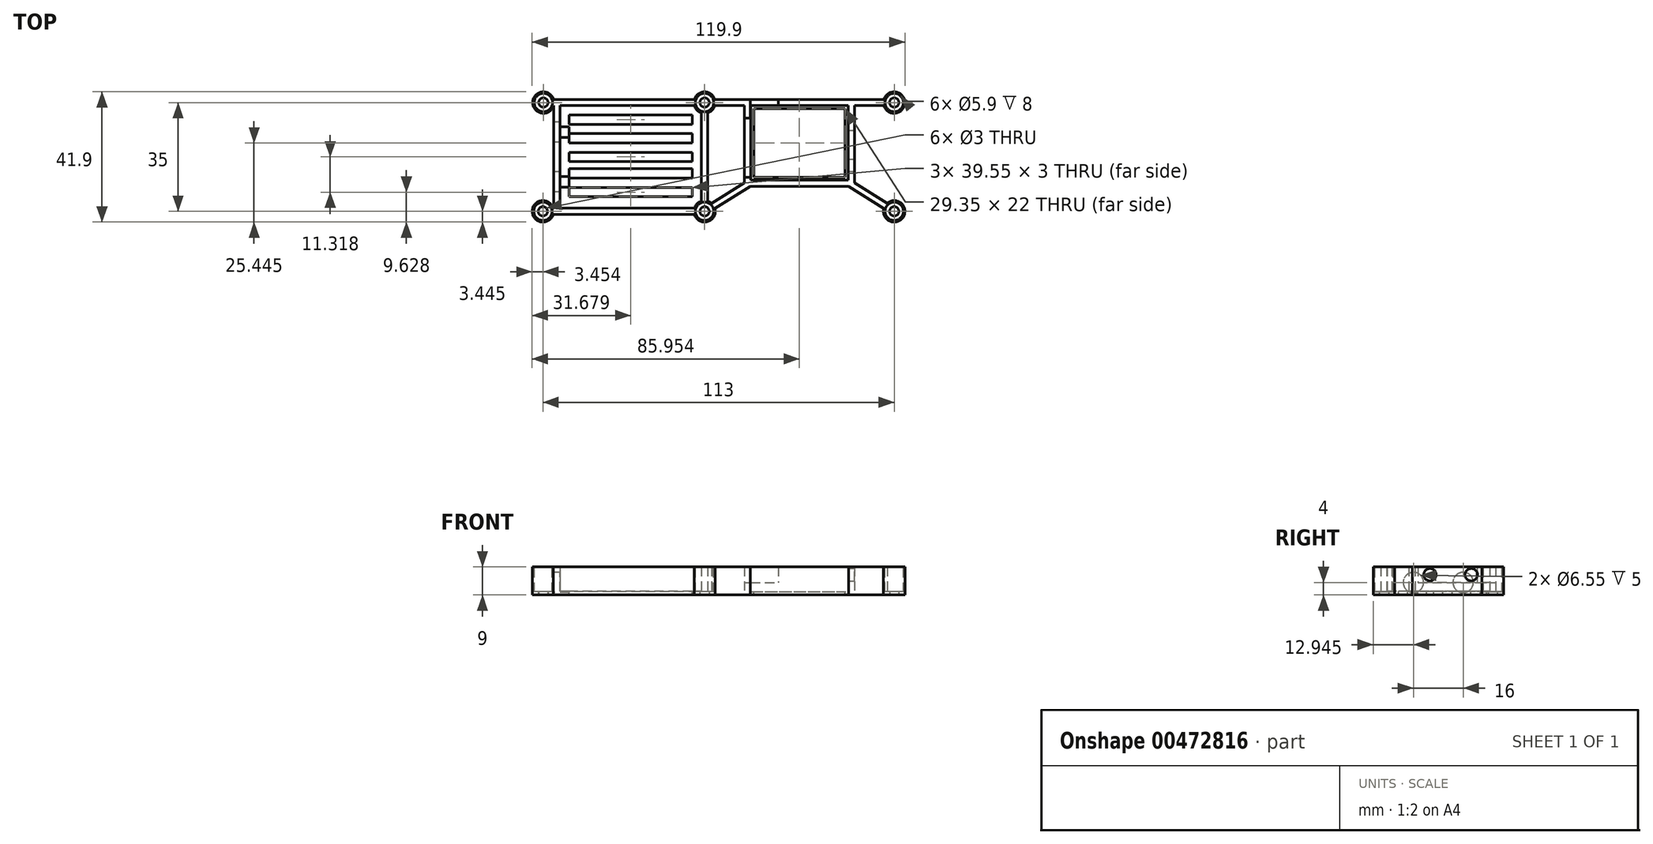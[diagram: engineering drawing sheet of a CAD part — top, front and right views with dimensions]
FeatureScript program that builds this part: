
annotation { "Feature Type Name" : "Feature", "Feature Type Description" : "" }
export const myFeature = defineFeature(function(context is Context, id is Id, definition is map)
    precondition{}
    {
        {
            var Q0;
            Q0=qCreatedBy(makeId("Top.planeOp"),FACE);
            var sketch = newSketch(context, id + "F0", { "sketchPlane" : qUnion([Q0])});
            skLineSegment(sketch, "E0.bottom", {"start": v(59.75, 20.2) * mm, "end": v(-53.1, 20.2) * mm, "construction": true});
            skLineSegment(sketch, "E0.top", {"start": v(59.75, -14.8) * mm, "end": v(-53.25, -14.8) * mm, "construction": true});
            skLineSegment(sketch, "E0.left", {"start": v(59.75, 20.2) * mm, "end": v(59.75, -14.8) * mm, "construction": true});
            skCircle(sketch, "E1", {"center": v(59.75, 20.2) * mm, "radius": 1.5 * mm});
            skCircle(sketch, "E2", {"center": v(59.75, -14.8) * mm, "radius": 1.5 * mm});
            skLineSegment(sketch, "E3.bottom", {"start": v(59.75, 20.2) * mm, "end": v(-1.25, 20.2) * mm, "construction": true});
            skLineSegment(sketch, "E3.top", {"start": v(59.75, -14.8) * mm, "end": v(-1.25, -14.8) * mm, "construction": true});
            skLineSegment(sketch, "E3.right", {"start": v(-1.25, 20.2) * mm, "end": v(-1.25, -14.8) * mm, "construction": true});
            skCircle(sketch, "E4", {"center": v(-1.25, 20.2) * mm, "radius": 1.5 * mm});
            skCircle(sketch, "E5", {"center": v(-1.25, -14.8) * mm, "radius": 1.5 * mm});
            skCircle(sketch, "E6", {"center": v(-53.1, 20.2) * mm, "radius": 1.5 * mm});
            skCircle(sketch, "E7", {"center": v(-53.25, -14.8) * mm, "radius": 1.5 * mm});
            skCircle(sketch, "E8", {"center": v(-1.25, 20.2) * mm, "radius": 3.45 * mm});
            skCircle(sketch, "E9", {"center": v(-1.25, -14.8) * mm, "radius": 3.45 * mm});
            skCircle(sketch, "E10", {"center": v(59.75, -14.8) * mm, "radius": 3.45 * mm});
            skCircle(sketch, "E11", {"center": v(-53.25, -14.8) * mm, "radius": 3.45 * mm});
            skCircle(sketch, "E12", {"center": v(-53.1, 20.2) * mm, "radius": 3.45 * mm});
            skCircle(sketch, "E13", {"center": v(59.75, 20.2) * mm, "radius": 3.45 * mm});
            skLineSegment(sketch, "E14.bottom", {"start": v(13.58, 19.2) * mm, "end": v(44.93, 19.2) * mm});
            skLineSegment(sketch, "E14.top", {"start": v(13.58, -4.8) * mm, "end": v(44.93, -4.8) * mm});
            skLineSegment(sketch, "E14.left", {"start": v(13.58, 19.2) * mm, "end": v(13.58, -4.8) * mm});
            skLineSegment(sketch, "E14.right", {"start": v(44.93, 19.2) * mm, "end": v(44.93, -4.8) * mm});
            skLineSegment(sketch, "E15", {"start": v(29.25, 20.2) * mm, "end": v(29.25, -14.8) * mm, "construction": true});
            skLineSegment(sketch, "E16.bottom", {"start": v(11.58, 21.2) * mm, "end": v(46.93, 21.2) * mm});
            skLineSegment(sketch, "E16.top", {"start": v(11.58, -6.8) * mm, "end": v(46.93, -6.8) * mm});
            skLineSegment(sketch, "E16.left", {"start": v(11.58, 21.2) * mm, "end": v(11.58, -6.8) * mm});
            skLineSegment(sketch, "E16.right", {"start": v(46.93, 21.2) * mm, "end": v(46.93, -6.8) * mm});
            skLineSegment(sketch, "E17", {"start": v(11.58, 21.2) * mm, "end": v(2.06, 21.2) * mm});
            skLineSegment(sketch, "E18", {"start": v(11.58, 19.2) * mm, "end": v(2.06, 19.2) * mm});
            skLineSegment(sketch, "E19", {"start": v(11.58, -5.63) * mm, "end": v(1.03, -12.2) * mm});
            skLineSegment(sketch, "E20", {"start": v(13.47, -6.8) * mm, "end": v(2.08, -13.9) * mm});
            skLineSegment(sketch, "E21", {"start": v(11.58, -6.8) * mm, "end": v(-1.25, -14.8) * mm, "construction": true});
            skLineSegment(sketch, "E22", {"start": v(59.75, -14.8) * mm, "end": v(46.93, -6.8) * mm, "construction": true});
            skLineSegment(sketch, "E23", {"start": v(46.93, -5.63) * mm, "end": v(57.48, -12.2) * mm});
            skLineSegment(sketch, "E24", {"start": v(45.04, -6.8) * mm, "end": v(56.42, -13.9) * mm});
            skLineSegment(sketch, "E25", {"start": v(46.93, 21.2) * mm, "end": v(56.45, 21.2) * mm});
            skLineSegment(sketch, "E26", {"start": v(44.93, 19.2) * mm, "end": v(56.45, 19.2) * mm});
            skLineSegment(sketch, "E27.bottom", {"start": v(-52.25, 19.2) * mm, "end": v(-2.25, 19.2) * mm});
            skLineSegment(sketch, "E27.top", {"start": v(-52.25, -13.8) * mm, "end": v(-2.36, -13.8) * mm});
            skLineSegment(sketch, "E27.right", {"start": v(-2.25, 19.2) * mm, "end": v(-2.25, -13.69) * mm});
            skLineSegment(sketch, "E28.bottom", {"start": v(-54.25, 21.2) * mm, "end": v(-0.25, 21.2) * mm});
            skLineSegment(sketch, "E28.top", {"start": v(-54.25, -15.8) * mm, "end": v(-0.25, -15.8) * mm});
            skLineSegment(sketch, "E28.right", {"start": v(-0.25, 21.2) * mm, "end": v(-0.25, -15.8) * mm});
            skLineSegment(sketch, "E29", {"start": v(-49.8, 19.2) * mm, "end": v(-49.8, -13.8) * mm});
            skLineSegment(sketch, "E30", {"start": v(-47.8, 19.2) * mm, "end": v(-47.8, -13.8) * mm});
            skCircle(sketch, "E31", {"center": v(-53.1, 20.2) * mm, "radius": 2.95 * mm});
            skCircle(sketch, "E32", {"center": v(-1.25, 20.2) * mm, "radius": 2.95 * mm});
            skCircle(sketch, "E33", {"center": v(59.75, 20.2) * mm, "radius": 2.95 * mm});
            skCircle(sketch, "E34", {"center": v(59.75, -14.8) * mm, "radius": 2.95 * mm});
            skCircle(sketch, "E35", {"center": v(-1.25, -14.8) * mm, "radius": 2.95 * mm});
            skCircle(sketch, "E36", {"center": v(-53.25, -14.8) * mm, "radius": 2.95 * mm});
            skSolve(sketch);
        }
        {
            var Q0;
            {var subQ1=sQuery(id+"F0.wireOp",EDGE,"E12");var subQ3=sQuery(id+"F0.wireOp",EDGE,"E28.bottom");var subQ4=makeQuery(id+"F0.imprint","INTERSECT",VERTEX,{"derivedFrom":[subQ1,subQ3]});Q0=makeQuery(id+"F0.imprint","IMPRINT",FACE,{"disambiguationData":[TD([[makeQuery(id+"F0.imprint","IMPRINT",EDGE,{"disambiguationData":[TD([[subQ4,1.0]])],"derivedFrom":subQ3}),1.0]])]});}
            var Q1;
            {var subQ1=sQuery(id+"F0.wireOp",EDGE,"E6");var subQ5=sQuery(id+"F0.wireOp",EDGE,"E28.bottom");var subQ7=makeQuery(id+"F0.imprint","INTERSECT",VERTEX,{"disambiguationData":[OD(0.0)],"derivedFrom":[subQ1,subQ5]});Q1=makeQuery(id+"F0.imprint","IMPRINT",FACE,{"disambiguationData":[TD([[makeQuery(id+"F0.imprint","IMPRINT",EDGE,{"disambiguationData":[TD([[subQ7,1.0]])],"derivedFrom":subQ1}),-1.0]])]});}
            var Q2;
            {var subQ0=sQuery(id+"F0.wireOp",EDGE,"E27.bottom");var subQ1=sQuery(id+"F0.wireOp",EDGE,"E6");var subQ2=makeQuery(id+"F0.imprint","INTERSECT",VERTEX,{"derivedFrom":[subQ1,subQ0]});Q2=makeQuery(id+"F0.imprint","IMPRINT",FACE,{"disambiguationData":[TD([[makeQuery(id+"F0.imprint","IMPRINT",EDGE,{"disambiguationData":[TD([[subQ2,-1.0]])],"derivedFrom":subQ1}),-1.0]])]});}
            var Q3;
            {var subQ1=sQuery(id+"F0.wireOp",EDGE,"E12");var subQ3=sQuery(id+"F0.wireOp",EDGE,"E28.bottom");var subQ4=makeQuery(id+"F0.imprint","INTERSECT",VERTEX,{"derivedFrom":[subQ1,subQ3]});Q3=makeQuery(id+"F0.imprint","IMPRINT",FACE,{"disambiguationData":[TD([[makeQuery(id+"F0.imprint","IMPRINT",EDGE,{"disambiguationData":[TD([[subQ4,1.0]])],"derivedFrom":subQ3}),-1.0]])]});}
            var Q4;
            {var subQ0=sQuery(id+"F0.wireOp",EDGE,"E29");Q4=makeQuery(id+"F0.imprint","IMPRINT",FACE,{"disambiguationData":[TD([[makeQuery(id+"F0.imprint","IMPRINT",EDGE,{"derivedFrom":subQ0}),1.0]])]});}
            var Q5;
            {var subQ2=sQuery(id+"F0.wireOp",EDGE,"E8");var subQ4=sQuery(id+"F0.wireOp",EDGE,"E28.bottom");var subQ5=makeQuery(id+"F0.imprint","INTERSECT",VERTEX,{"derivedFrom":[subQ2,subQ4]});Q5=makeQuery(id+"F0.imprint","IMPRINT",FACE,{"disambiguationData":[TD([[makeQuery(id+"F0.imprint","IMPRINT",EDGE,{"disambiguationData":[TD([[subQ5,-1.0]])],"derivedFrom":subQ2}),-1.0]])]});}
            var Q6;
            {var subQ0=sQuery(id+"F0.wireOp",EDGE,"E27.top");var subQ1=sQuery(id+"F0.wireOp",EDGE,"E7");var subQ2=makeQuery(id+"F0.imprint","INTERSECT",VERTEX,{"derivedFrom":[subQ1,subQ0]});Q6=makeQuery(id+"F0.imprint","IMPRINT",FACE,{"disambiguationData":[TD([[makeQuery(id+"F0.imprint","IMPRINT",EDGE,{"disambiguationData":[TD([[subQ2,-1.0]])],"derivedFrom":subQ1}),-1.0]])]});}
            var Q7;
            {var subQ0=sQuery(id+"F0.wireOp",EDGE,"E27.top");var subQ1=sQuery(id+"F0.wireOp",EDGE,"E11");var subQ2=makeQuery(id+"F0.imprint","INTERSECT",VERTEX,{"derivedFrom":[subQ1,subQ0]});Q7=makeQuery(id+"F0.imprint","IMPRINT",FACE,{"disambiguationData":[TD([[makeQuery(id+"F0.imprint","IMPRINT",EDGE,{"disambiguationData":[TD([[subQ2,-1.0]])],"derivedFrom":subQ1}),1.0]])]});}
            var Q8;
            {var subQ0=sQuery(id+"F0.wireOp",EDGE,"E27.top");var subQ1=sQuery(id+"F0.wireOp",EDGE,"E7");var subQ2=makeQuery(id+"F0.imprint","INTERSECT",VERTEX,{"derivedFrom":[subQ1,subQ0]});Q8=makeQuery(id+"F0.imprint","IMPRINT",FACE,{"disambiguationData":[TD([[makeQuery(id+"F0.imprint","IMPRINT",EDGE,{"disambiguationData":[TD([[subQ2,1.0]])],"derivedFrom":subQ1}),-1.0]])]});}
            var Q9;
            {var subQ5=sQuery(id+"F0.wireOp",EDGE,"E28.top");var subQ6=sQuery(id+"F0.wireOp",EDGE,"E9");var subQ7=makeQuery(id+"F0.imprint","INTERSECT",VERTEX,{"derivedFrom":[subQ6,subQ5]});Q9=makeQuery(id+"F0.imprint","IMPRINT",FACE,{"disambiguationData":[TD([[makeQuery(id+"F0.imprint","IMPRINT",EDGE,{"disambiguationData":[TD([[subQ7,1.0]])],"derivedFrom":subQ6}),-1.0]])]});}
            var Q10;
            {var subQ0=sQuery(id+"F0.wireOp",EDGE,"E27.top");var subQ1=sQuery(id+"F0.wireOp",EDGE,"E11");var subQ2=makeQuery(id+"F0.imprint","INTERSECT",VERTEX,{"derivedFrom":[subQ1,subQ0]});Q10=makeQuery(id+"F0.imprint","IMPRINT",FACE,{"disambiguationData":[TD([[makeQuery(id+"F0.imprint","IMPRINT",EDGE,{"disambiguationData":[TD([[subQ2,1.0]])],"derivedFrom":subQ1}),1.0]])]});}
            var Q11;
            {var subQ0=sQuery(id+"F0.wireOp",EDGE,"E27.right");var subQ1=sQuery(id+"F0.wireOp",EDGE,"E8");var subQ2=makeQuery(id+"F0.imprint","INTERSECT",VERTEX,{"derivedFrom":[subQ1,subQ0]});Q11=makeQuery(id+"F0.imprint","IMPRINT",FACE,{"disambiguationData":[TD([[makeQuery(id+"F0.imprint","IMPRINT",EDGE,{"disambiguationData":[TD([[subQ2,-1.0]])],"derivedFrom":subQ1}),-1.0]])]});}
            var Q12;
            {var subQ0=sQuery(id+"F0.wireOp",EDGE,"E17");Q12=makeQuery(id+"F0.imprint","IMPRINT",FACE,{"disambiguationData":[TD([[makeQuery(id+"F0.imprint","IMPRINT",EDGE,{"derivedFrom":subQ0}),1.0]])]});}
            var Q13;
            Q13=makeQuery(id+"F0.imprint","IMPRINT",FACE,{"disambiguationData":[TD([[makeQuery(id+"F0.imprint","IMPRINT",EDGE,{"derivedFrom":sQuery(id+"F0.wireOp",EDGE,"E14.bottom")}),1.0]])]});
            var Q14;
            {var subQ3=sQuery(id+"F0.wireOp",EDGE,"E19");Q14=makeQuery(id+"F0.imprint","IMPRINT",FACE,{"disambiguationData":[TD([[makeQuery(id+"F0.imprint","IMPRINT",EDGE,{"derivedFrom":subQ3}),1.0]])]});}
            var Q15;
            {var subQ0=sQuery(id+"F0.wireOp",EDGE,"E28.right");var subQ1=sQuery(id+"F0.wireOp",EDGE,"E5");var subQ2=makeQuery(id+"F0.imprint","INTERSECT",VERTEX,{"derivedFrom":[subQ1,subQ0]});Q15=makeQuery(id+"F0.imprint","IMPRINT",FACE,{"disambiguationData":[TD([[makeQuery(id+"F0.imprint","IMPRINT",EDGE,{"disambiguationData":[TD([[subQ2,1.0]])],"derivedFrom":subQ1}),-1.0]])]});}
            var Q16;
            {var subQ1=sQuery(id+"F0.wireOp",EDGE,"E9");var subQ5=makeQuery(id+"F0.imprint","INTERSECT",VERTEX,{"derivedFrom":[subQ1,sQuery(id+"F0.wireOp",EDGE,"E19")]});Q16=makeQuery(id+"F0.imprint","IMPRINT",FACE,{"disambiguationData":[TD([[makeQuery(id+"F0.imprint","IMPRINT",EDGE,{"disambiguationData":[TD([[subQ5,1.0]])],"derivedFrom":subQ1}),1.0]])]});}
            var Q17;
            {var subQ0=sQuery(id+"F0.wireOp",EDGE,"E27.right");var subQ1=sQuery(id+"F0.wireOp",EDGE,"E5");var subQ2=makeQuery(id+"F0.imprint","INTERSECT",VERTEX,{"derivedFrom":[subQ1,subQ0]});Q17=makeQuery(id+"F0.imprint","IMPRINT",FACE,{"disambiguationData":[TD([[makeQuery(id+"F0.imprint","IMPRINT",EDGE,{"disambiguationData":[TD([[subQ2,1.0]])],"derivedFrom":subQ1}),-1.0]])]});}
            var Q18;
            {var subQ0=sQuery(id+"F0.wireOp",EDGE,"E27.right");var subQ1=sQuery(id+"F0.wireOp",EDGE,"E9");var subQ2=makeQuery(id+"F0.imprint","INTERSECT",VERTEX,{"derivedFrom":[subQ1,subQ0]});Q18=makeQuery(id+"F0.imprint","IMPRINT",FACE,{"disambiguationData":[TD([[makeQuery(id+"F0.imprint","IMPRINT",EDGE,{"disambiguationData":[TD([[subQ2,-1.0]])],"derivedFrom":subQ1}),1.0]])]});}
            var Q19;
            {var subQ0=sQuery(id+"F0.wireOp",EDGE,"E28.right");var subQ1=sQuery(id+"F0.wireOp",EDGE,"E9");var subQ2=makeQuery(id+"F0.imprint","INTERSECT",VERTEX,{"derivedFrom":[subQ1,subQ0]});Q19=makeQuery(id+"F0.imprint","IMPRINT",FACE,{"disambiguationData":[TD([[makeQuery(id+"F0.imprint","IMPRINT",EDGE,{"disambiguationData":[TD([[subQ2,-1.0]])],"derivedFrom":subQ1}),1.0]])]});}
            var Q20;
            {var subQ0=sQuery(id+"F0.wireOp",EDGE,"E27.right");var subQ1=sQuery(id+"F0.wireOp",EDGE,"E5");var subQ2=makeQuery(id+"F0.imprint","INTERSECT",VERTEX,{"derivedFrom":[subQ1,subQ0]});Q20=makeQuery(id+"F0.imprint","IMPRINT",FACE,{"disambiguationData":[TD([[makeQuery(id+"F0.imprint","IMPRINT",EDGE,{"disambiguationData":[TD([[subQ2,-1.0]])],"derivedFrom":subQ1}),-1.0]])]});}
            var Q21;
            {var subQ0=sQuery(id+"F0.wireOp",EDGE,"E27.top");var subQ1=sQuery(id+"F0.wireOp",EDGE,"E5");var subQ2=makeQuery(id+"F0.imprint","INTERSECT",VERTEX,{"derivedFrom":[subQ1,subQ0]});Q21=makeQuery(id+"F0.imprint","IMPRINT",FACE,{"disambiguationData":[TD([[makeQuery(id+"F0.imprint","IMPRINT",EDGE,{"disambiguationData":[TD([[subQ2,-1.0]])],"derivedFrom":subQ1}),-1.0]])]});}
            var Q22;
            {var subQ0=sQuery(id+"F0.wireOp",EDGE,"E28.top");var subQ1=sQuery(id+"F0.wireOp",EDGE,"E9");var subQ2=makeQuery(id+"F0.imprint","INTERSECT",VERTEX,{"derivedFrom":[subQ1,subQ0]});Q22=makeQuery(id+"F0.imprint","IMPRINT",FACE,{"disambiguationData":[TD([[makeQuery(id+"F0.imprint","IMPRINT",EDGE,{"disambiguationData":[TD([[subQ2,1.0]])],"derivedFrom":subQ1}),1.0]])]});}
            var Q23;
            {var subQ0=sQuery(id+"F0.wireOp",EDGE,"E28.bottom");var subQ1=sQuery(id+"F0.wireOp",EDGE,"E4");var subQ2=makeQuery(id+"F0.imprint","INTERSECT",VERTEX,{"derivedFrom":[subQ1,subQ0]});Q23=makeQuery(id+"F0.imprint","IMPRINT",FACE,{"disambiguationData":[TD([[makeQuery(id+"F0.imprint","IMPRINT",EDGE,{"disambiguationData":[TD([[subQ2,1.0]])],"derivedFrom":subQ1}),-1.0]])]});}
            var Q24;
            {var subQ1=sQuery(id+"F0.wireOp",EDGE,"E8");var subQ9=makeQuery(id+"F0.imprint","INTERSECT",VERTEX,{"derivedFrom":[subQ1,sQuery(id+"F0.wireOp",EDGE,"E17")]});Q24=makeQuery(id+"F0.imprint","IMPRINT",FACE,{"disambiguationData":[TD([[makeQuery(id+"F0.imprint","IMPRINT",EDGE,{"disambiguationData":[TD([[subQ9,-1.0]])],"derivedFrom":subQ1}),1.0]])]});}
            var Q25;
            {var subQ0=sQuery(id+"F0.wireOp",EDGE,"E27.bottom");var subQ1=sQuery(id+"F0.wireOp",EDGE,"E8");var subQ2=makeQuery(id+"F0.imprint","INTERSECT",VERTEX,{"derivedFrom":[subQ1,subQ0]});Q25=makeQuery(id+"F0.imprint","IMPRINT",FACE,{"disambiguationData":[TD([[makeQuery(id+"F0.imprint","IMPRINT",EDGE,{"disambiguationData":[TD([[subQ2,-1.0]])],"derivedFrom":subQ1}),1.0]])]});}
            var Q26;
            {var subQ0=sQuery(id+"F0.wireOp",EDGE,"E28.bottom");var subQ1=sQuery(id+"F0.wireOp",EDGE,"E8");var subQ2=makeQuery(id+"F0.imprint","INTERSECT",VERTEX,{"derivedFrom":[subQ1,subQ0]});Q26=makeQuery(id+"F0.imprint","IMPRINT",FACE,{"disambiguationData":[TD([[makeQuery(id+"F0.imprint","IMPRINT",EDGE,{"disambiguationData":[TD([[subQ2,-1.0]])],"derivedFrom":subQ1}),1.0]])]});}
            var Q27;
            {var subQ0=sQuery(id+"F0.wireOp",EDGE,"E27.bottom");var subQ1=sQuery(id+"F0.wireOp",EDGE,"E4");var subQ2=makeQuery(id+"F0.imprint","INTERSECT",VERTEX,{"derivedFrom":[subQ1,subQ0]});Q27=makeQuery(id+"F0.imprint","IMPRINT",FACE,{"disambiguationData":[TD([[makeQuery(id+"F0.imprint","IMPRINT",EDGE,{"disambiguationData":[TD([[subQ2,1.0]])],"derivedFrom":subQ1}),-1.0]])]});}
            var Q28;
            {var subQ0=sQuery(id+"F0.wireOp",EDGE,"E27.bottom");var subQ1=sQuery(id+"F0.wireOp",EDGE,"E4");var subQ2=makeQuery(id+"F0.imprint","INTERSECT",VERTEX,{"derivedFrom":[subQ1,subQ0]});Q28=makeQuery(id+"F0.imprint","IMPRINT",FACE,{"disambiguationData":[TD([[makeQuery(id+"F0.imprint","IMPRINT",EDGE,{"disambiguationData":[TD([[subQ2,-1.0]])],"derivedFrom":subQ1}),-1.0]])]});}
            var Q29;
            {var subQ0=sQuery(id+"F0.wireOp",EDGE,"E27.right");var subQ1=sQuery(id+"F0.wireOp",EDGE,"E4");var subQ2=makeQuery(id+"F0.imprint","INTERSECT",VERTEX,{"derivedFrom":[subQ1,subQ0]});Q29=makeQuery(id+"F0.imprint","IMPRINT",FACE,{"disambiguationData":[TD([[makeQuery(id+"F0.imprint","IMPRINT",EDGE,{"disambiguationData":[TD([[subQ2,-1.0]])],"derivedFrom":subQ1}),-1.0]])]});}
            var Q30;
            {var subQ0=sQuery(id+"F0.wireOp",EDGE,"E27.right");var subQ1=sQuery(id+"F0.wireOp",EDGE,"E8");var subQ2=makeQuery(id+"F0.imprint","INTERSECT",VERTEX,{"derivedFrom":[subQ1,subQ0]});Q30=makeQuery(id+"F0.imprint","IMPRINT",FACE,{"disambiguationData":[TD([[makeQuery(id+"F0.imprint","IMPRINT",EDGE,{"disambiguationData":[TD([[subQ2,-1.0]])],"derivedFrom":subQ1}),1.0]])]});}
            var Q31;
            {var subQ0=sQuery(id+"F0.wireOp",EDGE,"E25");Q31=makeQuery(id+"F0.imprint","IMPRINT",FACE,{"disambiguationData":[TD([[makeQuery(id+"F0.imprint","IMPRINT",EDGE,{"derivedFrom":subQ0}),-1.0]])]});}
            var Q32;
            Q32=makeQuery(id+"F0.imprint","IMPRINT",FACE,{"disambiguationData":[TD([[makeQuery(id+"F0.imprint","IMPRINT",EDGE,{"derivedFrom":sQuery(id+"F0.wireOp",EDGE,"E1")}),-1.0]])]});
            var Q33;
            Q33=makeQuery(id+"F0.imprint","IMPRINT",FACE,{"disambiguationData":[TD([[makeQuery(id+"F0.imprint","IMPRINT",EDGE,{"derivedFrom":sQuery(id+"F0.wireOp",EDGE,"E33")}),-1.0]])]});
            var Q34;
            {var subQ0=sQuery(id+"F0.wireOp",EDGE,"E23");Q34=makeQuery(id+"F0.imprint","IMPRINT",FACE,{"disambiguationData":[TD([[makeQuery(id+"F0.imprint","IMPRINT",EDGE,{"derivedFrom":subQ0}),-1.0]])]});}
            var Q35;
            Q35=makeQuery(id+"F0.imprint","IMPRINT",FACE,{"disambiguationData":[TD([[makeQuery(id+"F0.imprint","IMPRINT",EDGE,{"derivedFrom":sQuery(id+"F0.wireOp",EDGE,"E2")}),-1.0]])]});
            var Q36;
            Q36=makeQuery(id+"F0.imprint","IMPRINT",FACE,{"disambiguationData":[TD([[makeQuery(id+"F0.imprint","IMPRINT",EDGE,{"derivedFrom":sQuery(id+"F0.wireOp",EDGE,"E34")}),-1.0]])]});
            var Q37;
            Q37=makeQuery(id+"F0.imprint","IMPRINT",FACE,{"disambiguationData":[TD([[makeQuery(id+"F0.imprint","IMPRINT",EDGE,{"derivedFrom":sQuery(id+"F0.wireOp",EDGE,"E2")}),1.0]])]});
            var Q38;
            Q38=makeQuery(id+"F0.imprint","IMPRINT",FACE,{"disambiguationData":[TD([[makeQuery(id+"F0.imprint","IMPRINT",EDGE,{"derivedFrom":sQuery(id+"F0.wireOp",EDGE,"E1")}),1.0]])]});
            var Q39;
            {var subQ0=sQuery(id+"F0.wireOp",EDGE,"E27.right");var subQ3=sQuery(id+"F0.wireOp",EDGE,"E5");var subQ4=makeQuery(id+"F0.imprint","INTERSECT",VERTEX,{"derivedFrom":[subQ3,subQ0]});Q39=makeQuery(id+"F0.imprint","IMPRINT",FACE,{"disambiguationData":[TD([[makeQuery(id+"F0.imprint","IMPRINT",EDGE,{"disambiguationData":[TD([[subQ4,1.0]])],"derivedFrom":subQ3}),1.0]])]});}
            var Q40;
            {var subQ0=sQuery(id+"F0.wireOp",EDGE,"E28.right");var subQ1=sQuery(id+"F0.wireOp",EDGE,"E5");var subQ2=makeQuery(id+"F0.imprint","INTERSECT",VERTEX,{"derivedFrom":[subQ1,subQ0]});Q40=makeQuery(id+"F0.imprint","IMPRINT",FACE,{"disambiguationData":[TD([[makeQuery(id+"F0.imprint","IMPRINT",EDGE,{"disambiguationData":[TD([[subQ2,1.0]])],"derivedFrom":subQ1}),1.0]])]});}
            var Q41;
            {var subQ1=sQuery(id+"F0.wireOp",EDGE,"E27.bottom");var subQ3=sQuery(id+"F0.wireOp",EDGE,"E4");var subQ4=makeQuery(id+"F0.imprint","INTERSECT",VERTEX,{"derivedFrom":[subQ3,subQ1]});Q41=makeQuery(id+"F0.imprint","IMPRINT",FACE,{"disambiguationData":[TD([[makeQuery(id+"F0.imprint","IMPRINT",EDGE,{"disambiguationData":[TD([[subQ4,1.0]])],"derivedFrom":subQ3}),1.0]])]});}
            var Q42;
            {var subQ0=sQuery(id+"F0.wireOp",EDGE,"E28.bottom");var subQ1=sQuery(id+"F0.wireOp",EDGE,"E4");var subQ2=makeQuery(id+"F0.imprint","INTERSECT",VERTEX,{"derivedFrom":[subQ1,subQ0]});Q42=makeQuery(id+"F0.imprint","IMPRINT",FACE,{"disambiguationData":[TD([[makeQuery(id+"F0.imprint","IMPRINT",EDGE,{"disambiguationData":[TD([[subQ2,1.0]])],"derivedFrom":subQ1}),1.0]])]});}
            var Q43;
            {var subQ0=sQuery(id+"F0.wireOp",EDGE,"E27.bottom");var subQ1=sQuery(id+"F0.wireOp",EDGE,"E4");var subQ2=makeQuery(id+"F0.imprint","INTERSECT",VERTEX,{"derivedFrom":[subQ1,subQ0]});Q43=makeQuery(id+"F0.imprint","IMPRINT",FACE,{"disambiguationData":[TD([[makeQuery(id+"F0.imprint","IMPRINT",EDGE,{"disambiguationData":[TD([[subQ2,-1.0]])],"derivedFrom":subQ1}),1.0]])]});}
            var Q44;
            {var subQ0=sQuery(id+"F0.wireOp",EDGE,"E28.bottom");var subQ1=sQuery(id+"F0.wireOp",EDGE,"E6");var subQ2=makeQuery(id+"F0.imprint","INTERSECT",VERTEX,{"disambiguationData":[OD(0.0)],"derivedFrom":[subQ1,subQ0]});Q44=makeQuery(id+"F0.imprint","IMPRINT",FACE,{"disambiguationData":[TD([[makeQuery(id+"F0.imprint","IMPRINT",EDGE,{"disambiguationData":[TD([[subQ2,-1.0]])],"derivedFrom":subQ1}),1.0]])]});}
            var Q45;
            {var subQ0=sQuery(id+"F0.wireOp",EDGE,"E28.bottom");var subQ1=sQuery(id+"F0.wireOp",EDGE,"E6");var subQ2=makeQuery(id+"F0.imprint","INTERSECT",VERTEX,{"disambiguationData":[OD(0.0)],"derivedFrom":[subQ1,subQ0]});Q45=makeQuery(id+"F0.imprint","IMPRINT",FACE,{"disambiguationData":[TD([[makeQuery(id+"F0.imprint","IMPRINT",EDGE,{"disambiguationData":[TD([[subQ2,1.0]])],"derivedFrom":subQ1}),1.0]])]});}
            var Q46;
            {var subQ0=sQuery(id+"F0.wireOp",EDGE,"E7");var subQ1=makeQuery(id+"F0.imprint","INTERSECT",VERTEX,{"derivedFrom":[subQ0,sQuery(id+"F0.wireOp",EDGE,"E27.top")]});Q46=makeQuery(id+"F0.imprint","IMPRINT",FACE,{"disambiguationData":[TD([[makeQuery(id+"F0.imprint","IMPRINT",EDGE,{"disambiguationData":[TD([[subQ1,-1.0]])],"derivedFrom":subQ0}),1.0]])]});}
            extrude(context, id + "F1", {"entities" : qUnion([Q0, Q1, Q2, Q3, Q4, Q5, Q6, Q7, Q8, Q9, Q10, Q11, Q12, Q13, Q14, Q15, Q16, Q17, Q18, Q19, Q20, Q21, Q22, Q23, Q24, Q25, Q26, Q27, Q28, Q29, Q30, Q31, Q32, Q33, Q34, Q35, Q36, Q37, Q38, Q39, Q40, Q41, Q42, Q43, Q44, Q45, Q46]), "depth" : 9 * mm});
        }
        {
            var Q0;
            Q0=makeQuery(id+"F0.imprint","IMPRINT",FACE,{"disambiguationData":[TD([[makeQuery(id+"F0.imprint","IMPRINT",EDGE,{"derivedFrom":sQuery(id+"F0.wireOp",EDGE,"E14.bottom")}),-1.0]])]});
            extrude(context, id + "F2", {"entities" : qUnion([Q0]), "operationType" : NewBodyOperationType.ADD, "depth" : 1 * mm});
        }
        {
            var Q0;
            Q0=makeQuery(id+"F2.opExtrude","CAP_FACE",FACE,{"disambiguationData":[OSD([sQuery(id+"F0.wireOp",EDGE,"E14.bottom"),sQuery(id+"F0.wireOp",EDGE,"E14.top"),sQuery(id+"F0.wireOp",EDGE,"E14.left"),sQuery(id+"F0.wireOp",EDGE,"E14.right")])],"isStart":false});
            var sketch = newSketch(context, id + "F3", { "sketchPlane" : qUnion([Q0])});
            skLineSegment(sketch, "E37.bottom", {"start": v(14.58, 18.2) * mm, "end": v(43.93, 18.2) * mm});
            skLineSegment(sketch, "E37.top", {"start": v(14.58, -3.8) * mm, "end": v(43.93, -3.8) * mm});
            skLineSegment(sketch, "E37.left", {"start": v(14.58, 18.2) * mm, "end": v(14.58, -3.8) * mm});
            skLineSegment(sketch, "E37.right", {"start": v(43.93, 18.2) * mm, "end": v(43.93, -3.8) * mm});
            skSolve(sketch);
        }
        {
            var Q0;
            Q0=makeQuery(id+"F3.imprint","IMPRINT",FACE,{"disambiguationData":[TD([[makeQuery(id+"F3.imprint","IMPRINT",EDGE,{"derivedFrom":sQuery(id+"F3.wireOp",EDGE,"E37.bottom")}),-1.0]])]});
            extrude(context, id + "F4", {"entities" : qUnion([Q0]), "operationType" : NewBodyOperationType.REMOVE, "oppositeDirection" : true, "depth" : 25 * mm});
        }
        {
            var Q0;
            {var subQ0=sQuery(id+"F0.wireOp",EDGE,"E30");Q0=makeQuery(id+"F0.imprint","IMPRINT",FACE,{"disambiguationData":[TD([[makeQuery(id+"F0.imprint","IMPRINT",EDGE,{"derivedFrom":subQ0}),1.0]])]});}
            extrude(context, id + "F5", {"entities" : qUnion([Q0]), "operationType" : NewBodyOperationType.ADD, "depth" : 1.2 * mm});
        }
        {
            var Q0;
            Q0=makeQuery(id+"F5.opExtrude","CAP_FACE",FACE,{"disambiguationData":[OSD([sQuery(id+"F0.wireOp",EDGE,"E8"),sQuery(id+"F0.wireOp",EDGE,"E9"),sQuery(id+"F0.wireOp",EDGE,"E27.bottom"),sQuery(id+"F0.wireOp",EDGE,"E27.top"),sQuery(id+"F0.wireOp",EDGE,"E27.right"),sQuery(id+"F0.wireOp",EDGE,"E30")])],"isStart":false});
            var sketch = newSketch(context, id + "F6", { "sketchPlane" : qUnion([Q0])});
            skLineSegment(sketch, "E38.bottom", {"start": v(-44.8, 16.2) * mm, "end": v(-5.25, 16.2) * mm});
            skLineSegment(sketch, "E38.top", {"start": v(-44.8, 13.2) * mm, "end": v(-5.25, 13.2) * mm});
            skLineSegment(sketch, "E38.left", {"start": v(-44.8, 16.2) * mm, "end": v(-44.8, 13.2) * mm});
            skLineSegment(sketch, "E38.right", {"start": v(-5.25, 16.2) * mm, "end": v(-5.25, 13.2) * mm});
            skLineSegment(sketch, "E39.bottom", {"start": v(-5.25, 10.2) * mm, "end": v(-44.8, 10.2) * mm});
            skLineSegment(sketch, "E39.top", {"start": v(-5.25, 7.2) * mm, "end": v(-44.8, 7.2) * mm});
            skLineSegment(sketch, "E39.left", {"start": v(-5.25, 10.2) * mm, "end": v(-5.25, 7.2) * mm});
            skLineSegment(sketch, "E39.right", {"start": v(-44.8, 10.2) * mm, "end": v(-44.8, 7.2) * mm});
            skLineSegment(sketch, "E40.bottom", {"start": v(-5.25, 4.2) * mm, "end": v(-44.8, 4.2) * mm});
            skLineSegment(sketch, "E40.top", {"start": v(-5.25, 1.2) * mm, "end": v(-44.8, 1.2) * mm});
            skLineSegment(sketch, "E40.left", {"start": v(-5.25, 4.2) * mm, "end": v(-5.25, 1.2) * mm});
            skLineSegment(sketch, "E40.right", {"start": v(-44.8, 4.2) * mm, "end": v(-44.8, 1.2) * mm});
            skLineSegment(sketch, "E41.bottom", {"start": v(-5.25, -1.12) * mm, "end": v(-44.8, -1.12) * mm});
            skLineSegment(sketch, "E41.top", {"start": v(-5.25, -4.12) * mm, "end": v(-44.8, -4.12) * mm});
            skLineSegment(sketch, "E41.left", {"start": v(-5.25, -1.12) * mm, "end": v(-5.25, -4.12) * mm});
            skLineSegment(sketch, "E41.right", {"start": v(-44.8, -1.12) * mm, "end": v(-44.8, -4.12) * mm});
            skLineSegment(sketch, "E42.bottom", {"start": v(-5.25, -7.12) * mm, "end": v(-44.8, -7.12) * mm});
            skLineSegment(sketch, "E42.top", {"start": v(-5.25, -10.12) * mm, "end": v(-44.8, -10.12) * mm});
            skLineSegment(sketch, "E42.left", {"start": v(-5.25, -7.12) * mm, "end": v(-5.25, -10.12) * mm});
            skLineSegment(sketch, "E42.right", {"start": v(-44.8, -7.12) * mm, "end": v(-44.8, -10.12) * mm});
            skSolve(sketch);
        }
        {
            var Q0;
            Q0=makeQuery(id+"F6.imprint","IMPRINT",FACE,{"disambiguationData":[TD([[makeQuery(id+"F6.imprint","IMPRINT",EDGE,{"derivedFrom":sQuery(id+"F6.wireOp",EDGE,"E38.bottom")}),-1.0]])]});
            var Q1;
            Q1=makeQuery(id+"F6.imprint","IMPRINT",FACE,{"disambiguationData":[TD([[makeQuery(id+"F6.imprint","IMPRINT",EDGE,{"derivedFrom":sQuery(id+"F6.wireOp",EDGE,"E39.bottom")}),1.0]])]});
            var Q2;
            Q2=makeQuery(id+"F6.imprint","IMPRINT",FACE,{"disambiguationData":[TD([[makeQuery(id+"F6.imprint","IMPRINT",EDGE,{"derivedFrom":sQuery(id+"F6.wireOp",EDGE,"E40.bottom")}),1.0]])]});
            var Q3;
            Q3=makeQuery(id+"F6.imprint","IMPRINT",FACE,{"disambiguationData":[TD([[makeQuery(id+"F6.imprint","IMPRINT",EDGE,{"derivedFrom":sQuery(id+"F6.wireOp",EDGE,"E41.bottom")}),1.0]])]});
            var Q4;
            Q4=makeQuery(id+"F6.imprint","IMPRINT",FACE,{"disambiguationData":[TD([[makeQuery(id+"F6.imprint","IMPRINT",EDGE,{"derivedFrom":sQuery(id+"F6.wireOp",EDGE,"E42.bottom")}),1.0]])]});
            extrude(context, id + "F7", {"entities" : qUnion([Q0, Q1, Q2, Q3, Q4]), "operationType" : NewBodyOperationType.REMOVE, "oppositeDirection" : true, "depth" : 25 * mm});
        }
        {
            var Q0;
            Q0=makeQuery(id+"F1.opExtrude","SWEPT_FACE",FACE,{"disambiguationData":[OSD([sQuery(id+"F0.wireOp",EDGE,"E16.right")])]});
            var sketch = newSketch(context, id + "F8", { "sketchPlane" : qUnion([Q0])});
            skLineSegment(sketch, "E43", {"start": v(-5.63, 6.5) * mm, "end": v(19.2, 6.5) * mm, "construction": true});
            skLineSegment(sketch, "E44", {"start": v(-5.63, 6.5) * mm, "end": v(0, 6.5) * mm, "construction": true});
            skLineSegment(sketch, "E45", {"start": v(19.2, 6.5) * mm, "end": v(13.3, 6.5) * mm, "construction": true});
            skCircle(sketch, "E46", {"center": v(0, 6.5) * mm, "radius": 2 * mm});
            skCircle(sketch, "E47", {"center": v(13.3, 6.5) * mm, "radius": 2 * mm});
            skSolve(sketch);
        }
        {
            var Q0;
            Q0=makeQuery(id+"F8.imprint","IMPRINT",FACE,{"disambiguationData":[TD([[makeQuery(id+"F8.imprint","IMPRINT",EDGE,{"derivedFrom":sQuery(id+"F8.wireOp",EDGE,"E47")}),1.0]])]});
            var Q1;
            Q1=makeQuery(id+"F8.imprint","IMPRINT",FACE,{"disambiguationData":[TD([[makeQuery(id+"F8.imprint","IMPRINT",EDGE,{"derivedFrom":sQuery(id+"F8.wireOp",EDGE,"E46")}),1.0]])]});
            extrude(context, id + "F9", {"entities" : qUnion([Q0, Q1]), "operationType" : NewBodyOperationType.REMOVE, "oppositeDirection" : true, "depth" : 4 * mm});
        }
        {
            var Q0;
            Q0=makeQuery(id+"F1.opExtrude","SWEPT_FACE",FACE,{"disambiguationData":[OSD([sQuery(id+"F0.wireOp",EDGE,"E29")])]});
            var sketch = newSketch(context, id + "F10", { "sketchPlane" : qUnion([Q0])});
            skLineSegment(sketch, "E48", {"start": v(-2.7, 9) * mm, "end": v(-2.7, 0) * mm, "construction": true});
            skLineSegment(sketch, "E49", {"start": v(-10.7, 4) * mm, "end": v(5.3, 4) * mm, "construction": true});
            skCircle(sketch, "E50", {"center": v(-10.7, 4) * mm, "radius": 3.28 * mm});
            skCircle(sketch, "E51", {"center": v(5.3, 4) * mm, "radius": 3.28 * mm});
            skSolve(sketch);
        }
        {
            var Q0;
            Q0 = qSketchRegion(id + "F10", true);
            extrude(context, id + "F11", {"entities" : qUnion([Q0]), "operationType" : NewBodyOperationType.REMOVE, "oppositeDirection" : true, "depth" : 5 * mm});
        }
        {
            var Q0;
            Q0=makeQuery(id+"F10.imprint","IMPRINT",FACE,{"disambiguationData":[TD([[makeQuery(id+"F10.imprint","IMPRINT",EDGE,{"derivedFrom":sQuery(id+"F10.wireOp",EDGE,"E50")}),1.0]])]});
            var Q1;
            Q1=makeQuery(id+"F10.imprint","IMPRINT",FACE,{"disambiguationData":[TD([[makeQuery(id+"F10.imprint","IMPRINT",EDGE,{"derivedFrom":sQuery(id+"F10.wireOp",EDGE,"E51")}),1.0]])]});
            extrude(context, id + "F12", {"entities" : qUnion([Q0, Q1]), "operationType" : NewBodyOperationType.REMOVE, "oppositeDirection" : true, "depth" : 4 * mm});
        }
        {
            var Q0;
            {var subQ1=sQuery(id+"F0.wireOp",EDGE,"E6");var subQ5=sQuery(id+"F0.wireOp",EDGE,"E28.bottom");var subQ7=makeQuery(id+"F0.imprint","INTERSECT",VERTEX,{"disambiguationData":[OD(0.0)],"derivedFrom":[subQ1,subQ5]});Q0=makeQuery(id+"F0.imprint","IMPRINT",FACE,{"disambiguationData":[TD([[makeQuery(id+"F0.imprint","IMPRINT",EDGE,{"disambiguationData":[TD([[subQ7,1.0]])],"derivedFrom":subQ1}),-1.0]])]});}
            var Q1;
            {var subQ0=sQuery(id+"F0.wireOp",EDGE,"E28.bottom");var subQ1=sQuery(id+"F0.wireOp",EDGE,"E6");var subQ2=makeQuery(id+"F0.imprint","INTERSECT",VERTEX,{"disambiguationData":[OD(0.0)],"derivedFrom":[subQ1,subQ0]});Q1=makeQuery(id+"F0.imprint","IMPRINT",FACE,{"disambiguationData":[TD([[makeQuery(id+"F0.imprint","IMPRINT",EDGE,{"disambiguationData":[TD([[subQ2,-1.0]])],"derivedFrom":subQ1}),1.0]])]});}
            var Q2;
            {var subQ0=sQuery(id+"F0.wireOp",EDGE,"E27.bottom");var subQ1=sQuery(id+"F0.wireOp",EDGE,"E6");var subQ2=makeQuery(id+"F0.imprint","INTERSECT",VERTEX,{"derivedFrom":[subQ1,subQ0]});Q2=makeQuery(id+"F0.imprint","IMPRINT",FACE,{"disambiguationData":[TD([[makeQuery(id+"F0.imprint","IMPRINT",EDGE,{"disambiguationData":[TD([[subQ2,-1.0]])],"derivedFrom":subQ1}),-1.0]])]});}
            var Q3;
            {var subQ0=sQuery(id+"F0.wireOp",EDGE,"E28.bottom");var subQ1=sQuery(id+"F0.wireOp",EDGE,"E6");var subQ2=makeQuery(id+"F0.imprint","INTERSECT",VERTEX,{"disambiguationData":[OD(0.0)],"derivedFrom":[subQ1,subQ0]});Q3=makeQuery(id+"F0.imprint","IMPRINT",FACE,{"disambiguationData":[TD([[makeQuery(id+"F0.imprint","IMPRINT",EDGE,{"disambiguationData":[TD([[subQ2,1.0]])],"derivedFrom":subQ1}),1.0]])]});}
            var Q4;
            {var subQ0=sQuery(id+"F0.wireOp",EDGE,"E27.top");var subQ1=sQuery(id+"F0.wireOp",EDGE,"E7");var subQ2=makeQuery(id+"F0.imprint","INTERSECT",VERTEX,{"derivedFrom":[subQ1,subQ0]});Q4=makeQuery(id+"F0.imprint","IMPRINT",FACE,{"disambiguationData":[TD([[makeQuery(id+"F0.imprint","IMPRINT",EDGE,{"disambiguationData":[TD([[subQ2,-1.0]])],"derivedFrom":subQ1}),-1.0]])]});}
            var Q5;
            {var subQ0=sQuery(id+"F0.wireOp",EDGE,"E7");var subQ1=makeQuery(id+"F0.imprint","INTERSECT",VERTEX,{"derivedFrom":[subQ0,sQuery(id+"F0.wireOp",EDGE,"E27.top")]});Q5=makeQuery(id+"F0.imprint","IMPRINT",FACE,{"disambiguationData":[TD([[makeQuery(id+"F0.imprint","IMPRINT",EDGE,{"disambiguationData":[TD([[subQ1,-1.0]])],"derivedFrom":subQ0}),1.0]])]});}
            var Q6;
            {var subQ0=sQuery(id+"F0.wireOp",EDGE,"E27.top");var subQ1=sQuery(id+"F0.wireOp",EDGE,"E7");var subQ2=makeQuery(id+"F0.imprint","INTERSECT",VERTEX,{"derivedFrom":[subQ1,subQ0]});Q6=makeQuery(id+"F0.imprint","IMPRINT",FACE,{"disambiguationData":[TD([[makeQuery(id+"F0.imprint","IMPRINT",EDGE,{"disambiguationData":[TD([[subQ2,1.0]])],"derivedFrom":subQ1}),-1.0]])]});}
            var Q7;
            {var subQ0=sQuery(id+"F0.wireOp",EDGE,"E28.right");var subQ1=sQuery(id+"F0.wireOp",EDGE,"E5");var subQ2=makeQuery(id+"F0.imprint","INTERSECT",VERTEX,{"derivedFrom":[subQ1,subQ0]});Q7=makeQuery(id+"F0.imprint","IMPRINT",FACE,{"disambiguationData":[TD([[makeQuery(id+"F0.imprint","IMPRINT",EDGE,{"disambiguationData":[TD([[subQ2,1.0]])],"derivedFrom":subQ1}),-1.0]])]});}
            var Q8;
            {var subQ0=sQuery(id+"F0.wireOp",EDGE,"E27.right");var subQ1=sQuery(id+"F0.wireOp",EDGE,"E5");var subQ2=makeQuery(id+"F0.imprint","INTERSECT",VERTEX,{"derivedFrom":[subQ1,subQ0]});Q8=makeQuery(id+"F0.imprint","IMPRINT",FACE,{"disambiguationData":[TD([[makeQuery(id+"F0.imprint","IMPRINT",EDGE,{"disambiguationData":[TD([[subQ2,1.0]])],"derivedFrom":subQ1}),-1.0]])]});}
            var Q9;
            {var subQ0=sQuery(id+"F0.wireOp",EDGE,"E27.right");var subQ3=sQuery(id+"F0.wireOp",EDGE,"E5");var subQ4=makeQuery(id+"F0.imprint","INTERSECT",VERTEX,{"derivedFrom":[subQ3,subQ0]});Q9=makeQuery(id+"F0.imprint","IMPRINT",FACE,{"disambiguationData":[TD([[makeQuery(id+"F0.imprint","IMPRINT",EDGE,{"disambiguationData":[TD([[subQ4,1.0]])],"derivedFrom":subQ3}),1.0]])]});}
            var Q10;
            {var subQ0=sQuery(id+"F0.wireOp",EDGE,"E27.right");var subQ1=sQuery(id+"F0.wireOp",EDGE,"E5");var subQ2=makeQuery(id+"F0.imprint","INTERSECT",VERTEX,{"derivedFrom":[subQ1,subQ0]});Q10=makeQuery(id+"F0.imprint","IMPRINT",FACE,{"disambiguationData":[TD([[makeQuery(id+"F0.imprint","IMPRINT",EDGE,{"disambiguationData":[TD([[subQ2,-1.0]])],"derivedFrom":subQ1}),-1.0]])]});}
            var Q11;
            {var subQ0=sQuery(id+"F0.wireOp",EDGE,"E27.top");var subQ1=sQuery(id+"F0.wireOp",EDGE,"E5");var subQ2=makeQuery(id+"F0.imprint","INTERSECT",VERTEX,{"derivedFrom":[subQ1,subQ0]});Q11=makeQuery(id+"F0.imprint","IMPRINT",FACE,{"disambiguationData":[TD([[makeQuery(id+"F0.imprint","IMPRINT",EDGE,{"disambiguationData":[TD([[subQ2,-1.0]])],"derivedFrom":subQ1}),-1.0]])]});}
            var Q12;
            {var subQ0=sQuery(id+"F0.wireOp",EDGE,"E28.right");var subQ1=sQuery(id+"F0.wireOp",EDGE,"E5");var subQ2=makeQuery(id+"F0.imprint","INTERSECT",VERTEX,{"derivedFrom":[subQ1,subQ0]});Q12=makeQuery(id+"F0.imprint","IMPRINT",FACE,{"disambiguationData":[TD([[makeQuery(id+"F0.imprint","IMPRINT",EDGE,{"disambiguationData":[TD([[subQ2,1.0]])],"derivedFrom":subQ1}),1.0]])]});}
            var Q13;
            {var subQ0=sQuery(id+"F0.wireOp",EDGE,"E28.bottom");var subQ1=sQuery(id+"F0.wireOp",EDGE,"E4");var subQ2=makeQuery(id+"F0.imprint","INTERSECT",VERTEX,{"derivedFrom":[subQ1,subQ0]});Q13=makeQuery(id+"F0.imprint","IMPRINT",FACE,{"disambiguationData":[TD([[makeQuery(id+"F0.imprint","IMPRINT",EDGE,{"disambiguationData":[TD([[subQ2,1.0]])],"derivedFrom":subQ1}),-1.0]])]});}
            var Q14;
            {var subQ1=sQuery(id+"F0.wireOp",EDGE,"E27.bottom");var subQ3=sQuery(id+"F0.wireOp",EDGE,"E4");var subQ4=makeQuery(id+"F0.imprint","INTERSECT",VERTEX,{"derivedFrom":[subQ3,subQ1]});Q14=makeQuery(id+"F0.imprint","IMPRINT",FACE,{"disambiguationData":[TD([[makeQuery(id+"F0.imprint","IMPRINT",EDGE,{"disambiguationData":[TD([[subQ4,1.0]])],"derivedFrom":subQ3}),1.0]])]});}
            var Q15;
            {var subQ0=sQuery(id+"F0.wireOp",EDGE,"E28.bottom");var subQ1=sQuery(id+"F0.wireOp",EDGE,"E4");var subQ2=makeQuery(id+"F0.imprint","INTERSECT",VERTEX,{"derivedFrom":[subQ1,subQ0]});Q15=makeQuery(id+"F0.imprint","IMPRINT",FACE,{"disambiguationData":[TD([[makeQuery(id+"F0.imprint","IMPRINT",EDGE,{"disambiguationData":[TD([[subQ2,1.0]])],"derivedFrom":subQ1}),1.0]])]});}
            var Q16;
            {var subQ0=sQuery(id+"F0.wireOp",EDGE,"E27.bottom");var subQ1=sQuery(id+"F0.wireOp",EDGE,"E4");var subQ2=makeQuery(id+"F0.imprint","INTERSECT",VERTEX,{"derivedFrom":[subQ1,subQ0]});Q16=makeQuery(id+"F0.imprint","IMPRINT",FACE,{"disambiguationData":[TD([[makeQuery(id+"F0.imprint","IMPRINT",EDGE,{"disambiguationData":[TD([[subQ2,1.0]])],"derivedFrom":subQ1}),-1.0]])]});}
            var Q17;
            {var subQ0=sQuery(id+"F0.wireOp",EDGE,"E27.right");var subQ1=sQuery(id+"F0.wireOp",EDGE,"E4");var subQ2=makeQuery(id+"F0.imprint","INTERSECT",VERTEX,{"derivedFrom":[subQ1,subQ0]});Q17=makeQuery(id+"F0.imprint","IMPRINT",FACE,{"disambiguationData":[TD([[makeQuery(id+"F0.imprint","IMPRINT",EDGE,{"disambiguationData":[TD([[subQ2,-1.0]])],"derivedFrom":subQ1}),-1.0]])]});}
            var Q18;
            {var subQ0=sQuery(id+"F0.wireOp",EDGE,"E27.bottom");var subQ1=sQuery(id+"F0.wireOp",EDGE,"E4");var subQ2=makeQuery(id+"F0.imprint","INTERSECT",VERTEX,{"derivedFrom":[subQ1,subQ0]});Q18=makeQuery(id+"F0.imprint","IMPRINT",FACE,{"disambiguationData":[TD([[makeQuery(id+"F0.imprint","IMPRINT",EDGE,{"disambiguationData":[TD([[subQ2,-1.0]])],"derivedFrom":subQ1}),-1.0]])]});}
            var Q19;
            Q19=makeQuery(id+"F0.imprint","IMPRINT",FACE,{"disambiguationData":[TD([[makeQuery(id+"F0.imprint","IMPRINT",EDGE,{"derivedFrom":sQuery(id+"F0.wireOp",EDGE,"E1")}),-1.0]])]});
            var Q20;
            Q20=makeQuery(id+"F0.imprint","IMPRINT",FACE,{"disambiguationData":[TD([[makeQuery(id+"F0.imprint","IMPRINT",EDGE,{"derivedFrom":sQuery(id+"F0.wireOp",EDGE,"E1")}),1.0]])]});
            var Q21;
            Q21=makeQuery(id+"F0.imprint","IMPRINT",FACE,{"disambiguationData":[TD([[makeQuery(id+"F0.imprint","IMPRINT",EDGE,{"derivedFrom":sQuery(id+"F0.wireOp",EDGE,"E2")}),-1.0]])]});
            var Q22;
            Q22=makeQuery(id+"F0.imprint","IMPRINT",FACE,{"disambiguationData":[TD([[makeQuery(id+"F0.imprint","IMPRINT",EDGE,{"derivedFrom":sQuery(id+"F0.wireOp",EDGE,"E2")}),1.0]])]});
            extrude(context, id + "F13", {"entities" : qUnion([Q0, Q1, Q2, Q3, Q4, Q5, Q6, Q7, Q8, Q9, Q10, Q11, Q12, Q13, Q14, Q15, Q16, Q17, Q18, Q19, Q20, Q21, Q22]), "operationType" : NewBodyOperationType.REMOVE, "oppositeDirection" : true, "depth" : 9 * mm});
        }
        {
            var Q0;
            Q0=makeQuery(id+"F1.opExtrude","CAP_FACE",FACE,{"disambiguationData":[OSD([sQuery(id+"F0.wireOp",EDGE,"E5"),sQuery(id+"F0.wireOp",EDGE,"E8"),sQuery(id+"F0.wireOp",EDGE,"E9"),sQuery(id+"F0.wireOp",EDGE,"E10"),sQuery(id+"F0.wireOp",EDGE,"E11"),sQuery(id+"F0.wireOp",EDGE,"E12"),sQuery(id+"F0.wireOp",EDGE,"E13"),sQuery(id+"F0.wireOp",EDGE,"E14.bottom"),sQuery(id+"F0.wireOp",EDGE,"E14.top"),sQuery(id+"F0.wireOp",EDGE,"E14.left"),sQuery(id+"F0.wireOp",EDGE,"E14.right"),sQuery(id+"F0.wireOp",EDGE,"E16.bottom"),sQuery(id+"F0.wireOp",EDGE,"E16.top"),sQuery(id+"F0.wireOp",EDGE,"E16.left"),sQuery(id+"F0.wireOp",EDGE,"E16.right"),sQuery(id+"F0.wireOp",EDGE,"E17"),sQuery(id+"F0.wireOp",EDGE,"E18"),sQuery(id+"F0.wireOp",EDGE,"E19"),sQuery(id+"F0.wireOp",EDGE,"E20"),sQuery(id+"F0.wireOp",EDGE,"E23"),sQuery(id+"F0.wireOp",EDGE,"E24"),sQuery(id+"F0.wireOp",EDGE,"E25"),sQuery(id+"F0.wireOp",EDGE,"E26"),sQuery(id+"F0.wireOp",EDGE,"E27.bottom"),sQuery(id+"F0.wireOp",EDGE,"E27.top"),sQuery(id+"F0.wireOp",EDGE,"E27.right"),sQuery(id+"F0.wireOp",EDGE,"E28.bottom"),sQuery(id+"F0.wireOp",EDGE,"E28.top"),sQuery(id+"F0.wireOp",EDGE,"E28.right"),sQuery(id+"F0.wireOp",EDGE,"E29"),sQuery(id+"F0.wireOp",EDGE,"E30")])],"isStart":false});
            var sketch = newSketch(context, id + "F14", { "sketchPlane" : qUnion([Q0])});
            skCircle(sketch, "E52", {"center": v(-53.1, 20.2) * mm, "radius": 2.95 * mm});
            skCircle(sketch, "E53", {"center": v(-1.25, 20.2) * mm, "radius": 2.95 * mm});
            skCircle(sketch, "E54", {"center": v(59.75, 20.2) * mm, "radius": 2.95 * mm});
            skCircle(sketch, "E55", {"center": v(59.75, -14.8) * mm, "radius": 2.95 * mm});
            skCircle(sketch, "E56", {"center": v(-1.25, -14.8) * mm, "radius": 2.95 * mm});
            skCircle(sketch, "E57", {"center": v(-53.25, -14.8) * mm, "radius": 2.95 * mm});
            skSolve(sketch);
        }
        {
            var Q0;
            Q0=makeQuery(id+"F14.imprint","IMPRINT",FACE,{"disambiguationData":[TD([[makeQuery(id+"F14.imprint","IMPRINT",EDGE,{"derivedFrom":sQuery(id+"F14.wireOp",EDGE,"E57")}),1.0]])]});
            var Q1;
            Q1=makeQuery(id+"F14.imprint","IMPRINT",FACE,{"disambiguationData":[TD([[makeQuery(id+"F14.imprint","IMPRINT",EDGE,{"derivedFrom":sQuery(id+"F14.wireOp",EDGE,"E56")}),1.0]])]});
            var Q2;
            Q2=makeQuery(id+"F14.imprint","IMPRINT",FACE,{"disambiguationData":[TD([[makeQuery(id+"F14.imprint","IMPRINT",EDGE,{"derivedFrom":sQuery(id+"F14.wireOp",EDGE,"E52")}),1.0]])]});
            var Q3;
            Q3=makeQuery(id+"F14.imprint","IMPRINT",FACE,{"disambiguationData":[TD([[makeQuery(id+"F14.imprint","IMPRINT",EDGE,{"derivedFrom":sQuery(id+"F14.wireOp",EDGE,"E53")}),1.0]])]});
            var Q4;
            Q4=makeQuery(id+"F14.imprint","IMPRINT",FACE,{"disambiguationData":[TD([[makeQuery(id+"F14.imprint","IMPRINT",EDGE,{"derivedFrom":sQuery(id+"F14.wireOp",EDGE,"E54")}),1.0]])]});
            var Q5;
            Q5=makeQuery(id+"F14.imprint","IMPRINT",FACE,{"disambiguationData":[TD([[makeQuery(id+"F14.imprint","IMPRINT",EDGE,{"derivedFrom":sQuery(id+"F14.wireOp",EDGE,"E55")}),1.0]])]});
            extrude(context, id + "F15", {"entities" : qUnion([Q0, Q1, Q2, Q3, Q4, Q5]), "operationType" : NewBodyOperationType.REMOVE, "oppositeDirection" : true, "depth" : 8 * mm});
        }
        {
            var Q0;
            {var subQ0=sQuery(id+"F0.wireOp",EDGE,"E7");var subQ1=makeQuery(id+"F0.imprint","INTERSECT",VERTEX,{"derivedFrom":[subQ0,sQuery(id+"F0.wireOp",EDGE,"E27.top")]});Q0=makeQuery(id+"F0.imprint","IMPRINT",FACE,{"disambiguationData":[TD([[makeQuery(id+"F0.imprint","IMPRINT",EDGE,{"disambiguationData":[TD([[subQ1,-1.0]])],"derivedFrom":subQ0}),1.0]])]});}
            extrude(context, id + "F16", {"entities" : qUnion([Q0]), "operationType" : NewBodyOperationType.REMOVE, "depth" : 25 * mm});
        }
        {
            var Q0;
            {var subQ0=sQuery(id+"F0.wireOp",EDGE,"E28.bottom");var subQ1=sQuery(id+"F0.wireOp",EDGE,"E6");var subQ2=makeQuery(id+"F0.imprint","INTERSECT",VERTEX,{"disambiguationData":[OD(0.0)],"derivedFrom":[subQ1,subQ0]});Q0=makeQuery(id+"F0.imprint","IMPRINT",FACE,{"disambiguationData":[TD([[makeQuery(id+"F0.imprint","IMPRINT",EDGE,{"disambiguationData":[TD([[subQ2,-1.0]])],"derivedFrom":subQ1}),1.0]])]});}
            var Q1;
            {var subQ0=sQuery(id+"F0.wireOp",EDGE,"E28.bottom");var subQ1=sQuery(id+"F0.wireOp",EDGE,"E6");var subQ2=makeQuery(id+"F0.imprint","INTERSECT",VERTEX,{"disambiguationData":[OD(0.0)],"derivedFrom":[subQ1,subQ0]});Q1=makeQuery(id+"F0.imprint","IMPRINT",FACE,{"disambiguationData":[TD([[makeQuery(id+"F0.imprint","IMPRINT",EDGE,{"disambiguationData":[TD([[subQ2,1.0]])],"derivedFrom":subQ1}),1.0]])]});}
            extrude(context, id + "F17", {"entities" : qUnion([Q0, Q1]), "operationType" : NewBodyOperationType.REMOVE, "depth" : 25 * mm});
        }
        {
            var Q0;
            {var subQ1=sQuery(id+"F0.wireOp",EDGE,"E27.bottom");var subQ3=sQuery(id+"F0.wireOp",EDGE,"E4");var subQ5=makeQuery(id+"F0.imprint","INTERSECT",VERTEX,{"derivedFrom":[subQ3,subQ1]});Q0=makeQuery(id+"F0.imprint","IMPRINT",FACE,{"disambiguationData":[TD([[makeQuery(id+"F0.imprint","IMPRINT",EDGE,{"disambiguationData":[TD([[subQ5,1.0]])],"derivedFrom":subQ3}),1.0]])]});}
            var Q1;
            {var subQ0=sQuery(id+"F0.wireOp",EDGE,"E28.bottom");var subQ1=sQuery(id+"F0.wireOp",EDGE,"E4");var subQ2=makeQuery(id+"F0.imprint","INTERSECT",VERTEX,{"derivedFrom":[subQ1,subQ0]});Q1=makeQuery(id+"F0.imprint","IMPRINT",FACE,{"disambiguationData":[TD([[makeQuery(id+"F0.imprint","IMPRINT",EDGE,{"disambiguationData":[TD([[subQ2,1.0]])],"derivedFrom":subQ1}),1.0]])]});}
            var Q2;
            {var subQ0=sQuery(id+"F0.wireOp",EDGE,"E27.bottom");var subQ1=sQuery(id+"F0.wireOp",EDGE,"E4");var subQ2=makeQuery(id+"F0.imprint","INTERSECT",VERTEX,{"derivedFrom":[subQ1,subQ0]});Q2=makeQuery(id+"F0.imprint","IMPRINT",FACE,{"disambiguationData":[TD([[makeQuery(id+"F0.imprint","IMPRINT",EDGE,{"disambiguationData":[TD([[subQ2,-1.0]])],"derivedFrom":subQ1}),1.0]])]});}
            extrude(context, id + "F18", {"entities" : qUnion([Q0, Q1, Q2]), "operationType" : NewBodyOperationType.REMOVE, "depth" : 25 * mm});
        }
        {
            var Q0;
            {var subQ3=sQuery(id+"F0.wireOp",EDGE,"E5");var subQ7=makeQuery(id+"F0.imprint","INTERSECT",VERTEX,{"derivedFrom":[subQ3,sQuery(id+"F0.wireOp",EDGE,"E27.right")]});Q0=makeQuery(id+"F0.imprint","IMPRINT",FACE,{"disambiguationData":[TD([[makeQuery(id+"F0.imprint","IMPRINT",EDGE,{"disambiguationData":[TD([[subQ7,1.0]])],"derivedFrom":subQ3}),1.0]])]});}
            var Q1;
            {var subQ0=sQuery(id+"F0.wireOp",EDGE,"E28.right");var subQ1=sQuery(id+"F0.wireOp",EDGE,"E5");var subQ2=makeQuery(id+"F0.imprint","INTERSECT",VERTEX,{"derivedFrom":[subQ1,subQ0]});Q1=makeQuery(id+"F0.imprint","IMPRINT",FACE,{"disambiguationData":[TD([[makeQuery(id+"F0.imprint","IMPRINT",EDGE,{"disambiguationData":[TD([[subQ2,1.0]])],"derivedFrom":subQ1}),1.0]])]});}
            extrude(context, id + "F19", {"entities" : qUnion([Q0, Q1]), "operationType" : NewBodyOperationType.REMOVE, "depth" : 25 * mm});
        }
        {
            var Q0;
            Q0=makeQuery(id+"F0.imprint","IMPRINT",FACE,{"disambiguationData":[TD([[makeQuery(id+"F0.imprint","IMPRINT",EDGE,{"derivedFrom":sQuery(id+"F0.wireOp",EDGE,"E1")}),1.0]])]});
            var Q1;
            Q1=makeQuery(id+"F0.imprint","IMPRINT",FACE,{"disambiguationData":[TD([[makeQuery(id+"F0.imprint","IMPRINT",EDGE,{"derivedFrom":sQuery(id+"F0.wireOp",EDGE,"E2")}),1.0]])]});
            extrude(context, id + "F20", {"entities" : qUnion([Q0, Q1]), "operationType" : NewBodyOperationType.REMOVE, "depth" : 25 * mm});
        }
        {
            var Q0;
            Q0=makeQuery(id+"F1.opExtrude","SWEPT_FACE",FACE,{"disambiguationData":[OSD([sQuery(id+"F0.wireOp",EDGE,"E16.bottom"),sQuery(id+"F0.wireOp",EDGE,"E17"),sQuery(id+"F0.wireOp",EDGE,"E25")])]});
            var sketch = newSketch(context, id + "F21", { "sketchPlane" : qUnion([Q0])});
            skLineSegment(sketch, "E58.bottom", {"start": v(-13.51, 9) * mm, "end": v(-22.51, 9) * mm});
            skLineSegment(sketch, "E58.top", {"start": v(-13.51, 4) * mm, "end": v(-22.51, 4) * mm});
            skLineSegment(sketch, "E58.left", {"start": v(-13.51, 9) * mm, "end": v(-13.51, 4) * mm});
            skLineSegment(sketch, "E58.right", {"start": v(-22.51, 9) * mm, "end": v(-22.51, 4) * mm});
            skSolve(sketch);
        }
        {
            var Q0;
            Q0 = qSketchRegion(id + "F21", true);
            extrude(context, id + "F22", {"entities" : qUnion([Q0]), "operationType" : NewBodyOperationType.REMOVE, "oppositeDirection" : true, "depth" : 25 * mm});
        }
        {
            var Q0;
            Q0=makeQuery(id+"F22.boolean.opBoolean","COPY",FACE,{"derivedFrom":makeQuery(id+"F22.opExtrude","SWEPT_FACE",FACE,{"disambiguationData":[OSD([sQuery(id+"F21.wireOp",EDGE,"E58.left")])]})});
            var sketch = newSketch(context, id + "F23", { "sketchPlane" : qUnion([Q0])});
            skLineSegment(sketch, "E59.bottom", {"start": v(-3.8, 9) * mm, "end": v(15.2, 9) * mm});
            skLineSegment(sketch, "E59.top", {"start": v(-3.8, 4) * mm, "end": v(15.2, 4) * mm});
            skLineSegment(sketch, "E59.left", {"start": v(-3.8, 9) * mm, "end": v(-3.8, 4) * mm});
            skLineSegment(sketch, "E59.right", {"start": v(15.2, 9) * mm, "end": v(15.2, 4) * mm});
            skSolve(sketch);
        }
        {
            var Q0;
            Q0=makeQuery(id+"F23.imprint","IMPRINT",FACE,{"disambiguationData":[TD([[makeQuery(id+"F23.imprint","IMPRINT",EDGE,{"derivedFrom":sQuery(id+"F23.wireOp",EDGE,"E59.bottom")}),-1.0]])]});
            extrude(context, id + "F24", {"entities" : qUnion([Q0]), "operationType" : NewBodyOperationType.REMOVE, "oppositeDirection" : true, "depth" : 3 * mm});
        }
    });
